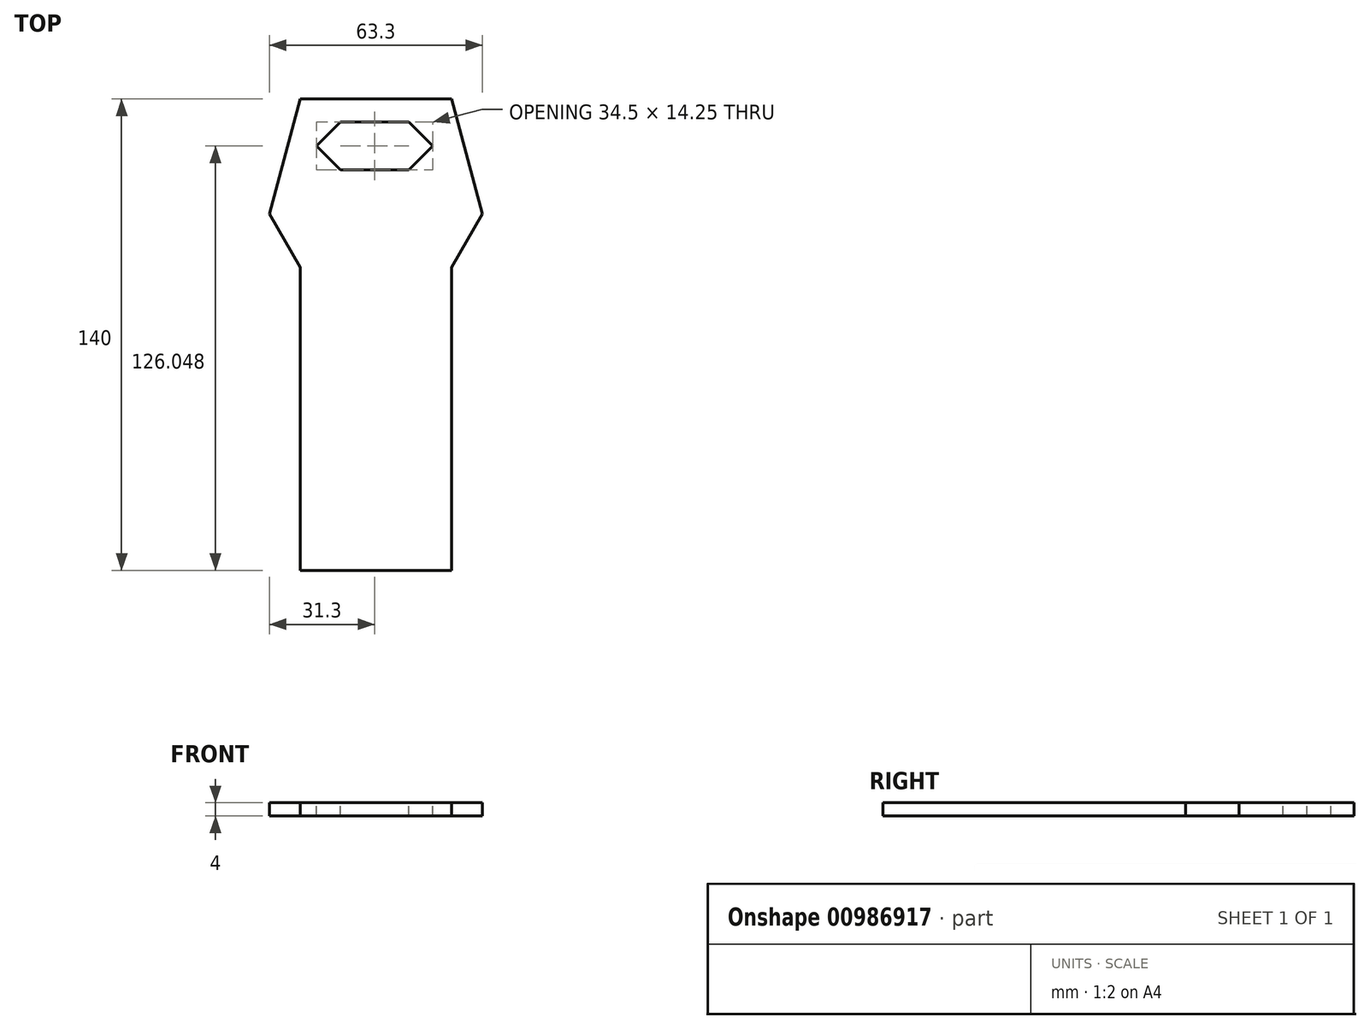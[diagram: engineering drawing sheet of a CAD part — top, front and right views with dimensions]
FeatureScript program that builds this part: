
annotation { "Feature Type Name" : "Feature", "Feature Type Description" : "" }
export const myFeature = defineFeature(function(context is Context, id is Id, definition is map)
    precondition{}
    {
        {
            var Q0;
            Q0=qCreatedBy(makeId("Top.planeOp"),FACE);
            var sketch = newSketch(context, id + "F0", { "sketchPlane" : qUnion([Q0])});
            skLineSegment(sketch, "E0.bottom", {"start": v(-22.5, 45) * mm, "end": v(22.5, 45) * mm});
            skLineSegment(sketch, "E0.top", {"start": v(-22.5, -45) * mm, "end": v(22.5, -45) * mm});
            skLineSegment(sketch, "E0.left", {"start": v(-22.5, 45) * mm, "end": v(-22.5, -45) * mm});
            skLineSegment(sketch, "E0.right", {"start": v(22.5, 45) * mm, "end": v(22.5, -45) * mm});
            skPoint(sketch, "E0.middle", {"position": v(0, 0) * mm});
            skLineSegment(sketch, "E1", {"start": v(-22.5, 45) * mm, "end": v(-31.65, 60.85) * mm});
            skLineSegment(sketch, "E2", {"start": v(-31.65, 60.85) * mm, "end": v(-22.5, 95) * mm});
            skLineSegment(sketch, "E3", {"start": v(-22.5, 95) * mm, "end": v(22.5, 95) * mm});
            skLineSegment(sketch, "E4", {"start": v(22.5, 95) * mm, "end": v(31.65, 60.85) * mm});
            skLineSegment(sketch, "E5", {"start": v(31.65, 60.85) * mm, "end": v(22.5, 45) * mm});
            skSolve(sketch);
        }
        {
            var Q0;
            Q0 = qSketchRegion(id + "F0", true);
            extrude(context, id + "F1", {"entities" : qUnion([Q0]), "depth" : 4 * mm, "offsetDistance" : 25 * mm});
        }
        {
            var Q0;
            Q0=makeQuery(id+"F1.opExtrude","CAP_FACE",FACE,{"disambiguationData":[OSD([sQuery(id+"F0.wireOp",EDGE,"E0.top"),sQuery(id+"F0.wireOp",EDGE,"E0.left"),sQuery(id+"F0.wireOp",EDGE,"E0.right"),sQuery(id+"F0.wireOp",EDGE,"E1"),sQuery(id+"F0.wireOp",EDGE,"E2"),sQuery(id+"F0.wireOp",EDGE,"E3"),sQuery(id+"F0.wireOp",EDGE,"E4"),sQuery(id+"F0.wireOp",EDGE,"E5")])],"isStart":false});
            var sketch = newSketch(context, id + "F2", { "sketchPlane" : qUnion([Q0])});
            skLineSegment(sketch, "E6", {"start": v(16.9, 81.05) * mm, "end": v(9.77, 73.92) * mm});
            skLineSegment(sketch, "E7", {"start": v(9.77, 73.92) * mm, "end": v(-10.48, 73.92) * mm});
            skLineSegment(sketch, "E8", {"start": v(-10.48, 73.92) * mm, "end": v(-17.6, 81.05) * mm});
            skLineSegment(sketch, "E9", {"start": v(-17.6, 81.05) * mm, "end": v(-10.48, 88.17) * mm});
            skLineSegment(sketch, "E10", {"start": v(-10.48, 88.17) * mm, "end": v(9.77, 88.17) * mm});
            skLineSegment(sketch, "E11", {"start": v(9.77, 88.17) * mm, "end": v(16.9, 81.05) * mm});
            skSolve(sketch);
        }
        {
            var Q0;
            Q0 = qSketchRegion(id + "F2", true);
            extrude(context, id + "F3", {"entities" : qUnion([Q0]), "operationType" : NewBodyOperationType.REMOVE, "endBound" : BoundingType.THROUGH_ALL, "oppositeDirection" : true, "depth" : 25 * mm, "offsetDistance" : 25 * mm});
        }
    });
